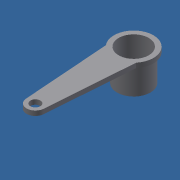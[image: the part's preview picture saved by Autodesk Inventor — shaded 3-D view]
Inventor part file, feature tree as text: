
AUTODESK INVENTOR PART (.ipt)
format: ipt  version: 2018 (Build 220112000, 112)  size: 108,032 bytes
history: native  units: mm
features: extrude x3, sketch x3
ambient origin geometry x8: Origin, YZ Plane, XZ Plane, XY Plane, X Axis, Y Axis, Z Axis, Center Point
bodies: Solid1 (feature_tree)
feature tree (6):
  extrude  "Extrusion1"  Depth=40.0mm
  extrude  "Extrusion2"  Depth=7.0mm TaperAngle=0.0deg
  extrude  "Extrusion3"  [1 undecoded]
  sketch  "Sketch1"  dims[d0=40.0mm d1=0.0mm d2=45.0mm]
  sketch  "Sketch2"  dims[d3=50.0mm d4=7.0mm d5=0.0mm]
  sketch  "Sketch3"  dims[d6=7.0mm d7=0.0mm]
note: 1 required parameter value undecoded (feature->parameter linkage not recoverable at this tier; creation-order binding heuristic only, values carry confidence <= 0.55)
